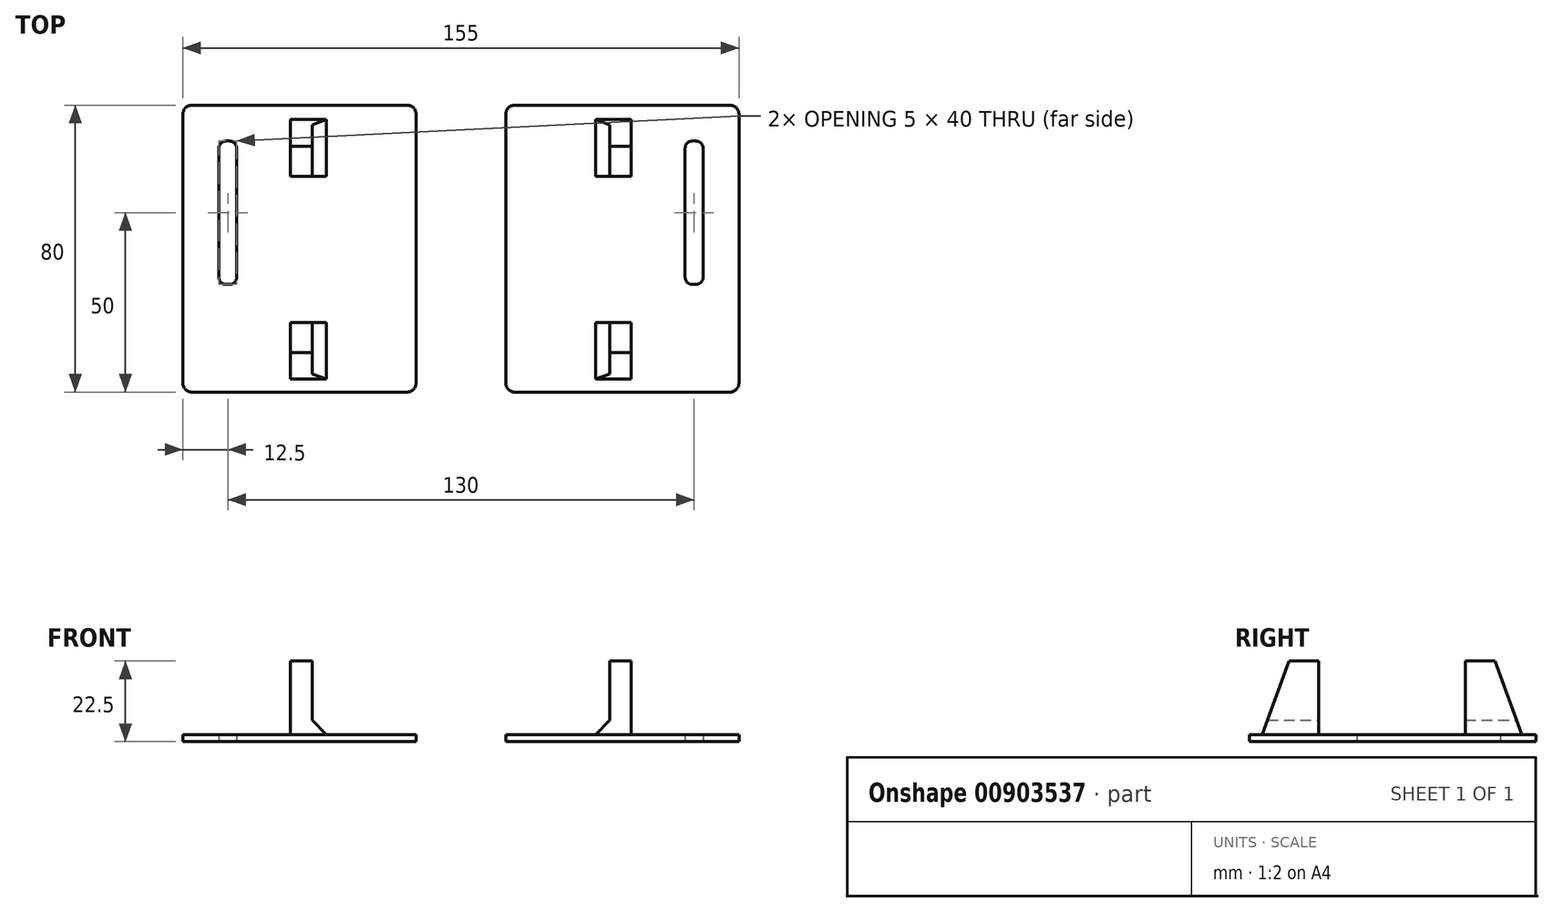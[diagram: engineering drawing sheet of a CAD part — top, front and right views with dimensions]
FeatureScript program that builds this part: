
annotation { "Feature Type Name" : "Feature", "Feature Type Description" : "" }
export const myFeature = defineFeature(function(context is Context, id is Id, definition is map)
    precondition{}
    {
        {
            var Q0;
            Q0=qCreatedBy(makeId("Top.planeOp"),FACE);
            var sketch = newSketch(context, id + "F0", { "sketchPlane" : qUnion([Q0])});
            skLineSegment(sketch, "E0.bottom", {"start": v(32.5, -40) * mm, "end": v(-32.5, -40) * mm});
            skLineSegment(sketch, "E0.top", {"start": v(32.5, 40) * mm, "end": v(-32.5, 40) * mm});
            skLineSegment(sketch, "E0.left", {"start": v(32.5, -40) * mm, "end": v(32.5, 40) * mm});
            skLineSegment(sketch, "E0.right", {"start": v(-32.5, -40) * mm, "end": v(-32.5, 40) * mm});
            skPoint(sketch, "E0.middle", {"position": v(0, 0) * mm});
            skLineSegment(sketch, "E1", {"start": v(0, 0) * mm, "end": v(0, 10) * mm, "construction": true});
            skLineSegment(sketch, "E2.bottom", {"start": v(-17.5, -10) * mm, "end": v(-22.5, -10) * mm});
            skLineSegment(sketch, "E2.top", {"start": v(-17.5, 30) * mm, "end": v(-22.5, 30) * mm});
            skLineSegment(sketch, "E2.left", {"start": v(-17.5, -10) * mm, "end": v(-17.5, 30) * mm});
            skLineSegment(sketch, "E2.right", {"start": v(-22.5, -10) * mm, "end": v(-22.5, 30) * mm});
            skPoint(sketch, "E2.middle", {"position": v(-20, 10) * mm});
            skLineSegment(sketch, "E3", {"start": v(-20, 10) * mm, "end": v(0, 10) * mm});
            skLineSegment(sketch, "E4.bottom", {"start": v(-2.5, 28) * mm, "end": v(3.5, 28) * mm});
            skLineSegment(sketch, "E4.top", {"start": v(-2.5, 20.2) * mm, "end": v(3.5, 20.2) * mm});
            skLineSegment(sketch, "E4.right", {"start": v(3.5, 28) * mm, "end": v(3.5, 20.2) * mm});
            skLineSegment(sketch, "E5.bottom", {"start": v(-2.5, -28.4) * mm, "end": v(3.5, -28.4) * mm});
            skLineSegment(sketch, "E5.top", {"start": v(-2.5, -20.6) * mm, "end": v(3.5, -20.6) * mm});
            skLineSegment(sketch, "E5.right", {"start": v(3.5, -28.4) * mm, "end": v(3.5, -20.6) * mm});
            skLineSegment(sketch, "E6", {"start": v(-2.5, -20.6) * mm, "end": v(-2.5, -28.4) * mm});
            skLineSegment(sketch, "E7", {"start": v(-2.5, 28) * mm, "end": v(-2.5, 20.2) * mm});
            skLineSegment(sketch, "E8", {"start": v(-2.5, -20.6) * mm, "end": v(-2.5, 20.2) * mm});
            skSolve(sketch);
        }
        {
            var Q0;
            {var subQ12=sQuery(id+"F0.wireOp",EDGE,"E0.left");Q0=makeQuery(id+"F0.imprint","IMPRINT",FACE,{"disambiguationData":[TD([[makeQuery(id+"F0.imprint","IMPRINT",EDGE,{"derivedFrom":subQ12}),1.0]])]});}
            var Q1;
            {var subQ10=sQuery(id+"F0.wireOp",EDGE,"E0.right");Q1=makeQuery(id+"F0.imprint","IMPRINT",FACE,{"disambiguationData":[TD([[makeQuery(id+"F0.imprint","IMPRINT",EDGE,{"derivedFrom":subQ10}),-1.0]])]});}
            var Q2;
            Q2=makeQuery(id+"F0.imprint","IMPRINT",FACE,{"disambiguationData":[TD([[makeQuery(id+"F0.imprint","IMPRINT",EDGE,{"derivedFrom":sQuery(id+"F0.wireOp",EDGE,"E5.bottom")}),1.0]])]});
            var Q3;
            Q3=makeQuery(id+"F0.imprint","IMPRINT",FACE,{"disambiguationData":[TD([[makeQuery(id+"F0.imprint","IMPRINT",EDGE,{"derivedFrom":sQuery(id+"F0.wireOp",EDGE,"E4.bottom")}),-1.0]])]});
            extrude(context, id + "F1", {"entities" : qUnion([Q0, Q1, Q2, Q3]), "depth" : 2 * mm, "offsetDistance" : 25 * mm});
        }
        {
            var Q0;
            Q0=makeQuery(id+"F0.imprint","IMPRINT",FACE,{"disambiguationData":[TD([[makeQuery(id+"F0.imprint","IMPRINT",EDGE,{"derivedFrom":sQuery(id+"F0.wireOp",EDGE,"E5.bottom")}),1.0]])]});
            var Q1;
            Q1=makeQuery(id+"F0.imprint","IMPRINT",FACE,{"disambiguationData":[TD([[makeQuery(id+"F0.imprint","IMPRINT",EDGE,{"derivedFrom":sQuery(id+"F0.wireOp",EDGE,"E4.bottom")}),-1.0]])]});
            extrude(context, id + "F2", {"entities" : qUnion([Q0, Q1]), "operationType" : NewBodyOperationType.ADD, "depth" : 22.5 * mm, "offsetDistance" : 25 * mm});
        }
        {
            var Q0;
            Q0=makeQuery(id+"F2.boolean.opBoolean","INTERSECT",EDGE,{"derivedFrom":[makeQuery(id+"F1.opExtrude","CAP_FACE",FACE,{"disambiguationData":[OSD([sQuery(id+"F0.wireOp",EDGE,"E0.bottom"),sQuery(id+"F0.wireOp",EDGE,"E0.top"),sQuery(id+"F0.wireOp",EDGE,"E0.left"),sQuery(id+"F0.wireOp",EDGE,"E0.right"),sQuery(id+"F0.wireOp",EDGE,"E2.bottom"),sQuery(id+"F0.wireOp",EDGE,"E2.top"),sQuery(id+"F0.wireOp",EDGE,"E2.left"),sQuery(id+"F0.wireOp",EDGE,"E2.right")])],"isStart":false}),makeQuery(id+"F2.opExtrude","SWEPT_FACE",FACE,{"disambiguationData":[OSD([sQuery(id+"F0.wireOp",EDGE,"E5.bottom")])]})]});
            var Q1;
            Q1=makeQuery(id+"F2.boolean.opBoolean","INTERSECT",EDGE,{"derivedFrom":[makeQuery(id+"F1.opExtrude","CAP_FACE",FACE,{"disambiguationData":[OSD([sQuery(id+"F0.wireOp",EDGE,"E0.bottom"),sQuery(id+"F0.wireOp",EDGE,"E0.top"),sQuery(id+"F0.wireOp",EDGE,"E0.left"),sQuery(id+"F0.wireOp",EDGE,"E0.right"),sQuery(id+"F0.wireOp",EDGE,"E2.bottom"),sQuery(id+"F0.wireOp",EDGE,"E2.top"),sQuery(id+"F0.wireOp",EDGE,"E2.left"),sQuery(id+"F0.wireOp",EDGE,"E2.right")])],"isStart":false}),makeQuery(id+"F2.opExtrude","SWEPT_FACE",FACE,{"disambiguationData":[OSD([sQuery(id+"F0.wireOp",EDGE,"E4.bottom")])]})]});
            chamfer(context, id + "F3", {"entities" : qUnion([Q0, Q1]), "chamferType" : ChamferType.OFFSET_ANGLE, "width" : 8 * mm, "oppositeDirection" : false, "angle" : 70 * degree, "tangentPropagation" : true});
        }
        {
            var Q0;
            Q0=makeQuery(id+"F2.boolean.opBoolean","INTERSECT",EDGE,{"derivedFrom":[makeQuery(id+"F1.opExtrude","CAP_FACE",FACE,{"disambiguationData":[OSD([sQuery(id+"F0.wireOp",EDGE,"E0.bottom"),sQuery(id+"F0.wireOp",EDGE,"E0.top"),sQuery(id+"F0.wireOp",EDGE,"E0.left"),sQuery(id+"F0.wireOp",EDGE,"E0.right"),sQuery(id+"F0.wireOp",EDGE,"E2.bottom"),sQuery(id+"F0.wireOp",EDGE,"E2.top"),sQuery(id+"F0.wireOp",EDGE,"E2.left"),sQuery(id+"F0.wireOp",EDGE,"E2.right")])],"isStart":false}),makeQuery(id+"F2.opExtrude","SWEPT_FACE",FACE,{"disambiguationData":[OSD([sQuery(id+"F0.wireOp",EDGE,"E5.right")])]})]});
            var Q1;
            Q1=makeQuery(id+"F2.boolean.opBoolean","INTERSECT",EDGE,{"derivedFrom":[makeQuery(id+"F1.opExtrude","CAP_FACE",FACE,{"disambiguationData":[OSD([sQuery(id+"F0.wireOp",EDGE,"E0.bottom"),sQuery(id+"F0.wireOp",EDGE,"E0.top"),sQuery(id+"F0.wireOp",EDGE,"E0.left"),sQuery(id+"F0.wireOp",EDGE,"E0.right"),sQuery(id+"F0.wireOp",EDGE,"E2.bottom"),sQuery(id+"F0.wireOp",EDGE,"E2.top"),sQuery(id+"F0.wireOp",EDGE,"E2.left"),sQuery(id+"F0.wireOp",EDGE,"E2.right")])],"isStart":false}),makeQuery(id+"F2.opExtrude","SWEPT_FACE",FACE,{"disambiguationData":[OSD([sQuery(id+"F0.wireOp",EDGE,"E4.right")])]})]});
            chamfer(context, id + "F4", {"entities" : qUnion([Q0, Q1]), "width" : 4 * mm, "tangentPropagation" : true});
        }
        {
            var Q0;
            Q0=makeQuery(id+"F1.opExtrude","SWEPT_EDGE",EDGE,{"disambiguationData":[OSD([sQuery(id+"F0.wireOp",EDGE,"E0.top"),sQuery(id+"F0.wireOp",EDGE,"E0.right")])]});
            var Q1;
            Q1=makeQuery(id+"F1.opExtrude","SWEPT_EDGE",EDGE,{"disambiguationData":[OSD([sQuery(id+"F0.wireOp",EDGE,"E0.top"),sQuery(id+"F0.wireOp",EDGE,"E0.left")])]});
            var Q2;
            Q2=makeQuery(id+"F1.opExtrude","SWEPT_EDGE",EDGE,{"disambiguationData":[OSD([sQuery(id+"F0.wireOp",EDGE,"E0.bottom"),sQuery(id+"F0.wireOp",EDGE,"E0.left")])]});
            var Q3;
            Q3=makeQuery(id+"F1.opExtrude","SWEPT_EDGE",EDGE,{"disambiguationData":[OSD([sQuery(id+"F0.wireOp",EDGE,"E0.bottom"),sQuery(id+"F0.wireOp",EDGE,"E0.right")])]});
            fillet(context, id + "F5", {"entities" : qUnion([Q0, Q1, Q2, Q3]), "radius" : 2.5 * mm, "tangentPropagation" : true, "allowEdgeOverflow" : false});
        }
        {
            var Q0;
            Q0=makeQuery(id+"F1.opExtrude","SWEPT_EDGE",EDGE,{"disambiguationData":[OSD([sQuery(id+"F0.wireOp",EDGE,"E2.top"),sQuery(id+"F0.wireOp",EDGE,"E2.left")])]});
            var Q1;
            Q1=makeQuery(id+"F1.opExtrude","SWEPT_EDGE",EDGE,{"disambiguationData":[OSD([sQuery(id+"F0.wireOp",EDGE,"E2.bottom"),sQuery(id+"F0.wireOp",EDGE,"E2.left")])]});
            var Q2;
            Q2=makeQuery(id+"F1.opExtrude","SWEPT_EDGE",EDGE,{"disambiguationData":[OSD([sQuery(id+"F0.wireOp",EDGE,"E2.bottom"),sQuery(id+"F0.wireOp",EDGE,"E2.right")])]});
            var Q3;
            Q3=makeQuery(id+"F1.opExtrude","SWEPT_EDGE",EDGE,{"disambiguationData":[OSD([sQuery(id+"F0.wireOp",EDGE,"E2.top"),sQuery(id+"F0.wireOp",EDGE,"E2.right")])]});
            fillet(context, id + "F6", {"entities" : qUnion([Q0, Q1, Q2, Q3]), "radius" : 2 * mm, "tangentPropagation" : true, "allowEdgeOverflow" : false});
        }
        {
            var Q0;
            Q0=makeQuery(id+"F1.opExtrude","SWEPT_BODY",BODY,{"disambiguationData":[OSD([sQuery(id+"F0.wireOp",EDGE,"E0.bottom"),sQuery(id+"F0.wireOp",EDGE,"E0.top"),sQuery(id+"F0.wireOp",EDGE,"E0.left"),sQuery(id+"F0.wireOp",EDGE,"E0.right"),sQuery(id+"F0.wireOp",EDGE,"E2.bottom"),sQuery(id+"F0.wireOp",EDGE,"E2.top"),sQuery(id+"F0.wireOp",EDGE,"E2.left"),sQuery(id+"F0.wireOp",EDGE,"E2.right")])]});
            var Q1;
            Q1=qCreatedBy(makeId("Right.planeOp"),FACE);
            mirror(context, id + "F7", {"entities" : qUnion([Q0]), "mirrorPlane" : qUnion([Q1])});
        }
        {
            var Q0;
            Q0=makeQuery(id+"F7.opPattern","COPY",BODY,{"derivedFrom":makeQuery(id+"F1.opExtrude","SWEPT_BODY",BODY,{"disambiguationData":[OSD([sQuery(id+"F0.wireOp",EDGE,"E0.bottom"),sQuery(id+"F0.wireOp",EDGE,"E0.top"),sQuery(id+"F0.wireOp",EDGE,"E0.left"),sQuery(id+"F0.wireOp",EDGE,"E0.right"),sQuery(id+"F0.wireOp",EDGE,"E2.bottom"),sQuery(id+"F0.wireOp",EDGE,"E2.top"),sQuery(id+"F0.wireOp",EDGE,"E2.left"),sQuery(id+"F0.wireOp",EDGE,"E2.right")])]}),"instanceName":"1"});
            transform(context, id + "F8", {"entities" : qUnion([Q0]), "transformType" : TransformType.TRANSLATION_3D, "dx" : 90 * mm, "dy" : 0 * mm, "dz" : 0 * mm, "makeCopy" : false});
        }
    });
